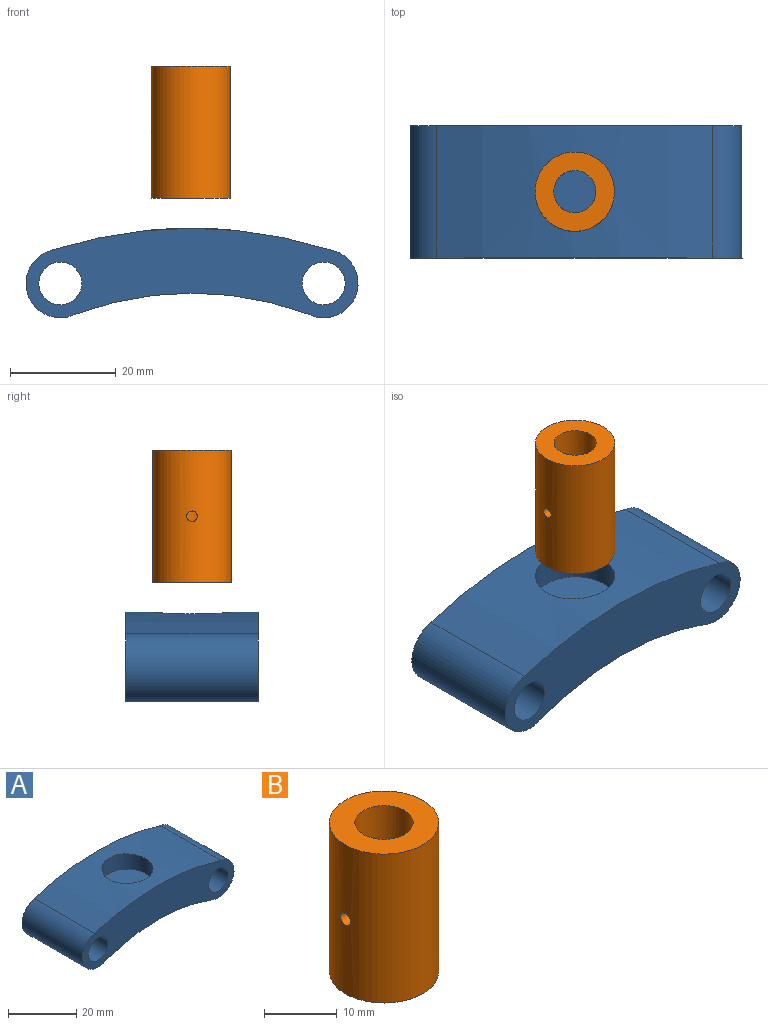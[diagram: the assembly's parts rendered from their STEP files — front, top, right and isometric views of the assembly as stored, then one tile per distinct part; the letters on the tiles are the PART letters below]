
ASSEMBLY  parts=2 mates=2
PART A: 10 faces, bbox 62.8x25x16.9 mm
  f0: cylinder r=86.01mm len=52.18mm, axis (0,1,0), area 1148.6mm2, adj f1,f3,f6,f7,f8
  f1: cylinder r=6.5mm len=25mm, axis (0,1,0), area 549.1mm2, adj f0,f2,f6,f7
  f2: cylinder r=62.65mm len=44.13mm, axis (0,1,0), area 1127.5mm2, adj f1,f3,f6,f7
  f3: cylinder r=6.5mm len=25mm, axis (0,1,0), area 560.8mm2, adj f0,f2,f6,f7
  f4: cylinder r=4.05mm len=25mm, axis (0,1,0), area 636.2mm2, adj f6,f7
  f5: cylinder r=4.05mm len=25mm, axis (0,1,0), area 636.2mm2, adj f6,f7
  f6: plane 62.84x16.94mm, normal (0,-1,0), area 664.3mm2, adj f0,f1,f2,f3,f4,f5
  f7: plane 62.84x16.94mm, normal (0,1,0), area 664.3mm2, adj f0,f1,f2,f3,f4,f5
  f8: cylinder r=7.5mm len=15mm, axis (0,0,-1), area 258.2mm2, adj f0,f9
  f9: plane 15x15mm, normal (0,0,1), area 176.7mm2, adj f8
PART B: 5 faces, bbox 15x15x25 mm
  f0: cylinder r=7.5mm len=25mm, axis (0,0,1), area 1175mm2, adj f2,f3,f4
  f1: cylinder r=4mm len=25mm, axis (0,0,-1), area 625.2mm2, adj f2,f3,f4
  f2: plane 15x15mm, normal (0,0,-1), area 126.4mm2, adj f0,f1
  f3: plane 15x15mm, normal (0,0,1), area 126.4mm2, adj f0,f1
  f4: cylinder r=1mm len=3.63mm, axis (1,0,0), area 22.2mm2, adj f0,f1
PLACE A t=(4.99,9.5,-46.19)mm
PLACE B t=(4.43,-3,-5.09)mm
MATE parallel B.f0 <-> A.f8  axis (0,0,1) through (4.43,-3,-30.09)mm
MATE slider B.f0 <-> A.f8  axis (0,0,1) through (4.43,-3,-17.59)mm
